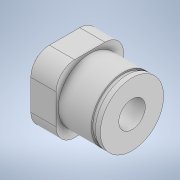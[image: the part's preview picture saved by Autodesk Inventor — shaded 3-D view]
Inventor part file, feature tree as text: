
AUTODESK INVENTOR PART (.ipt)
format: ipt  version: 2020 (Build 240168000, 168)  size: 341,504 bytes
history: native  units: mm
features: extrude x6, sketch x6, fillet x2
ambient origin geometry x8: Origin, YZ Plane, XZ Plane, XY Plane, X Axis, Y Axis, Z Axis, Center Point
bodies: Solid1 (feature_tree)
feature tree (14):
  extrude  "Extrusion1"  Depth=20.32mm
  extrude  "Extrusion2"  Depth=12.7mm
  fillet  "Fillet1"  Radius=12.7mm
  extrude  "Extrusion3"  Depth=5.588mm
  extrude  "Extrusion4"  Depth=1.5mm TaperAngle=0.0deg
  extrude  "Extrusion5"  Depth=25.0mm TaperAngle=0.0deg
  extrude  "Extrusion6"  Depth=5.0mm TaperAngle=0.0deg
  fillet  "Fillet2"  Radius=2.0mm
  sketch  "Sketch1"  dims[d0=20.32mm d1=20.32mm]
  sketch  "Sketch2"  dims[d2=7.62mm d3=0.0mm d4=19.05mm d5=12.7mm d6=0.0mm]
  sketch  "Sketch3"  dims[d7=5.588mm d8=18.25mm]
  sketch  "Sketch4"  dims[d9=2.72mm d10=0.0mm d11=1.5mm d12=0.0mm]
  sketch  "Sketch5"  dims[d13=8.0mm d14=25.0mm d15=0.0mm]
  sketch  "Sketch6"  dims[d16=10.0mm d17=5.0mm d18=0.0mm d19=2.0mm]
